# Revit family: rba-bim-b2908
name_source: partatom
category: Specialty Equipment
revit_build: Autodesk Revit 2018 (Build: 20170223_1515(x64)
units: mm (PartAtom-declared; Revit-internal decimal feet)

## family parameters
Cut with Voids When Loaded = No
Host = Face
OmniClass Number = 23.40.20.21
OmniClass Title = Toilet and Bath Specialties
Part Type = Normal
Room Calculation Point = No
Round Connector Dimension = Use Diameter
Shared = Yes

## types (2) — shared parameters
ADA Compliant = Yes
Assembly Code = C1030210
Default Elevation = 1.016
Frame Thickness = 0.019
Glass = 6.0mm Tempered Safety Glass
Height = 0.914
Keynote = 10 28 00
Model = B-2908 Series
Product Name = Glass Mirror with Stainless Steel Angle Frame
URL = www.rba.com.au

## per-type parameters (varying)
| type | Frame | Manufacturer | Modified Issue | Width |
| B-2908 1836 | Heavy Gauge #304 Stainless Steel | Bobrick Washroom Equipment | 20200514.01 | 0.457 |
| B-2908 2436 | <By Category> | RBA Group |  | 0.61 |

## geometry (parser evidence)
native form markers: Blend x2, Sweep x2
no freeform markers — native parametric forms only
